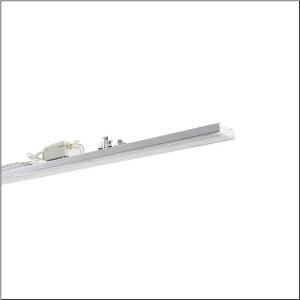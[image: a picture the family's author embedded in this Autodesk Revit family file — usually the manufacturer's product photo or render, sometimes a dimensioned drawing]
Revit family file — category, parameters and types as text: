
# Revit family: licross_r__21_recessed_mo_52tl12dv4fxg3c_6259
name_source: partatom
category: Lighting Fixtures
units: mm (PartAtom-declared; Revit-internal decimal feet)

## family parameters
Cut with Voids When Loaded = No
Host = Face
Light Source = No
Part Type = Normal
Room Calculation Point = No
Round Connector Dimension = Use Diameter
Shared = No

## types (1)
- --- (1 x LED, 950 lm, 5.5 W, 4000K)
    Apparent Load = 6 VA
    CIE Flux Codes = 72 92 99 100 100
    Color Rendering = 80
    Color Temperature = 4000K
    Default Elevation = 1800 mm
    Description = Licross® 21 Recessed MO, luminaire insert, of sheet steel, galvanised, coil coated, white, length: 2.250mm, width: 66mm, height: 67mm, LED rated luminous flux: 15.420lm, light colour: 840, control gear: DALI 2, with plug, 6-pole, with phase selection, for trunking rail, 14-core, mains connection: 220..240V, AC, 50/60Hz, rated input power: 89W, for trunking rail, 14-core, halogen-free wiring, for emergency light function, converter,control gear: single battery element, battery: LiFeP04, 9Ah, primary optical cover: cover, of PMMA, light emission: direct distribution, primary light characteristic: symmetric, protection rating (complete): IP40, insulation class (complete): insulation class I (protective earthing), certification: CE, UKCA, protection symbol: D if used in an environment without relevant dust loads with corresponding accessories, impact resistance: IK06, permissible ambient temperature for indoor applications: +5..+35°C, standard: EN 60598-2-22, LABS conformity tested according to VDMA 24364:2018-05, reducing of maximum allowable ambient temperature of 5°C with ceiling mounting, corresponds to IFS (International Featured Standards) requirements for safety and quality in the food industry, packaging unit: 1 piece
    Height = 58 mm
    Lamp = 1 x LED
    Lamp Light Flux = 950 lm
    Lamp Power = 5.5 W
    Lamp count = 1
    Length = 2250 mm
    Luminous efficacy = 173 lm/W
    Manufacturer = Siteco
    ModVariant = No
    Model = 52TL12DV4FXG3C
    Mounting Place = Ceiling
    Mounting Type = Pendant
    Number of Poles = 1
    OnlyDefault = Yes
    Power Factor = 1
    Product Name = Licross® 21 Recessed MO
    Product group = luminaire insert
    ProductGroupID = 901
    Protection Class = Protection class I
    Protection Degree = IP 40
    RLX_Detail_Level = 1
    RLX_Emergency_Light_Flux = 0 lm
    RLX_Emergency_Type = 0
    RLX_Emergency_Type_DB = No
    RlxData = <blob elided: 29841 chars, md5=6f57d96a>
    Socket = socket
    Standby Power = 0 W
    System Light Flux = 950 lm
    System Power = 6 W
    Type Comments = : emergency light operation: 3 h
    Type Image = l_1296930.jpg
    URL = http://relux.com
    VarID = @adj_040195
    Voltage = 0 V
    Weight = 0.00 kg
    Width = 66 mm

## geometry (parser evidence)
native form markers: Blend x4, Sweep x11
no freeform markers — native parametric forms only
